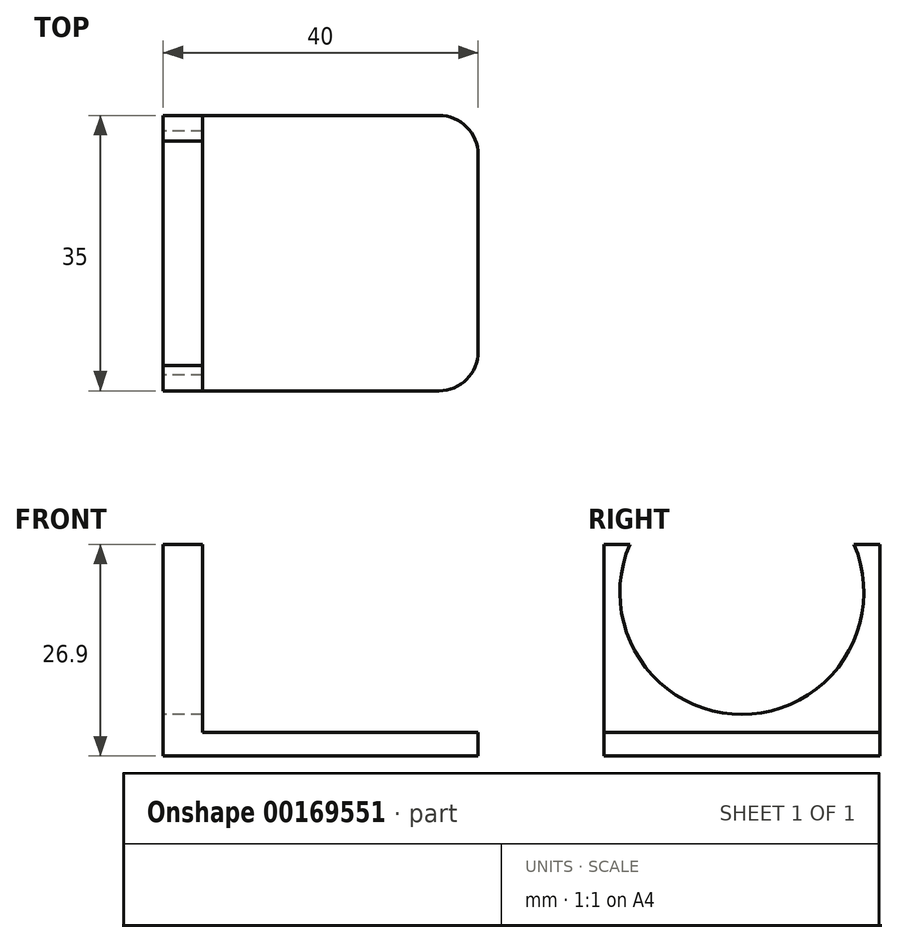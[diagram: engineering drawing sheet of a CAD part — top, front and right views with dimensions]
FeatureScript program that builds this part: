
annotation { "Feature Type Name" : "Feature", "Feature Type Description" : "" }
export const myFeature = defineFeature(function(context is Context, id is Id, definition is map)
    precondition{}
    {
        {
            var Q0;
            Q0=qCreatedBy(makeId("Top.planeOp"),FACE);
            var sketch = newSketch(context, id + "F0", { "sketchPlane" : qUnion([Q0])});
            skLineSegment(sketch, "E0.bottom", {"start": v(-20, 17.5) * mm, "end": v(20, 17.5) * mm});
            skLineSegment(sketch, "E0.top", {"start": v(-20, -17.5) * mm, "end": v(20, -17.5) * mm});
            skLineSegment(sketch, "E0.left", {"start": v(-20, 17.5) * mm, "end": v(-20, -17.5) * mm});
            skLineSegment(sketch, "E0.right", {"start": v(20, 17.5) * mm, "end": v(20, -17.5) * mm});
            skPoint(sketch, "E0.middle", {"position": v(0, 0) * mm});
            skSolve(sketch);
        }
        {
            var Q0;
            Q0=makeQuery(id+"F0.imprint","IMPRINT",FACE,{"disambiguationData":[TD([[makeQuery(id+"F0.imprint","IMPRINT",EDGE,{"derivedFrom":sQuery(id+"F0.wireOp",EDGE,"E0.bottom")}),-1.0]])]});
            extrude(context, id + "F1", {"entities" : qUnion([Q0]), "depth" : 3 * mm});
        }
        {
            var Q0;
            Q0=makeQuery(id+"F1.opExtrude","SWEPT_EDGE",EDGE,{"disambiguationData":[OSD([sQuery(id+"F0.wireOp",EDGE,"E0.bottom"),sQuery(id+"F0.wireOp",EDGE,"E0.right")])]});
            var Q1;
            Q1=makeQuery(id+"F1.opExtrude","SWEPT_EDGE",EDGE,{"disambiguationData":[OSD([sQuery(id+"F0.wireOp",EDGE,"E0.top"),sQuery(id+"F0.wireOp",EDGE,"E0.right")])]});
            fillet(context, id + "F2", {"entities" : qUnion([Q0, Q1]), "radius" : 5 * mm, "tangentPropagation" : true, "allowEdgeOverflow" : false});
        }
        {
            var Q0;
            Q0=makeQuery(id+"F1.opExtrude","CAP_FACE",FACE,{"disambiguationData":[OSD([sQuery(id+"F0.wireOp",EDGE,"E0.bottom"),sQuery(id+"F0.wireOp",EDGE,"E0.top"),sQuery(id+"F0.wireOp",EDGE,"E0.left"),sQuery(id+"F0.wireOp",EDGE,"E0.right")])],"isStart":false});
            var sketch = newSketch(context, id + "F3", { "sketchPlane" : qUnion([Q0])});
            skLineSegment(sketch, "E1.bottom", {"start": v(-20, 17.5) * mm, "end": v(-15, 17.5) * mm});
            skLineSegment(sketch, "E1.top", {"start": v(-20, -17.5) * mm, "end": v(-15, -17.5) * mm});
            skLineSegment(sketch, "E1.left", {"start": v(-20, 17.5) * mm, "end": v(-20, -17.5) * mm});
            skLineSegment(sketch, "E1.right", {"start": v(-15, 17.5) * mm, "end": v(-15, -17.5) * mm});
            skSolve(sketch);
        }
        {
            var Q0;
            Q0=makeQuery(id+"F3.imprint","IMPRINT",FACE,{"disambiguationData":[TD([[makeQuery(id+"F3.imprint","IMPRINT",EDGE,{"derivedFrom":sQuery(id+"F3.wireOp",EDGE,"E1.bottom")}),-1.0]])]});
            extrude(context, id + "F4", {"entities" : qUnion([Q0]), "operationType" : NewBodyOperationType.ADD, "depth" : 40 * mm});
        }
        {
            var Q0;
            Q0=makeQuery(id+"F4.boolean.opBoolean","MERGE",FACE,{"derivedFrom":[makeQuery(id+"F1.opExtrude","SWEPT_FACE",FACE,{"disambiguationData":[OSD([sQuery(id+"F0.wireOp",EDGE,"E0.left")])]}),makeQuery(id+"F4.opExtrude","SWEPT_FACE",FACE,{"disambiguationData":[OSD([sQuery(id+"F3.wireOp",EDGE,"E1.left")])]})]});
            var sketch = newSketch(context, id + "F5", { "sketchPlane" : qUnion([Q0])});
            skArc(sketch, "E2", {"start": v(-14.25, 26.9) * mm, "mid": v(0, 5.3) * mm, "end": v(14.25, 26.9) * mm});
            skLineSegment(sketch, "E3", {"start": v(-17.5, 26.9) * mm, "end": v(-14.25, 26.9) * mm});
            skLineSegment(sketch, "E4", {"start": v(14.25, 26.9) * mm, "end": v(17.5, 26.9) * mm});
            skSolve(sketch);
        }
        {
            var Q0;
            Q0=makeQuery(id+"F5.imprint","IMPRINT",FACE,{"disambiguationData":[TD([[makeQuery(id+"F5.imprint","IMPRINT",EDGE,{"derivedFrom":sQuery(id+"F5.wireOp",EDGE,"E2")}),1.0]])]});
            extrude(context, id + "F6", {"entities" : qUnion([Q0]), "operationType" : NewBodyOperationType.REMOVE, "endBound" : BoundingType.THROUGH_ALL, "oppositeDirection" : true, "depth" : 25 * mm});
        }
    });
